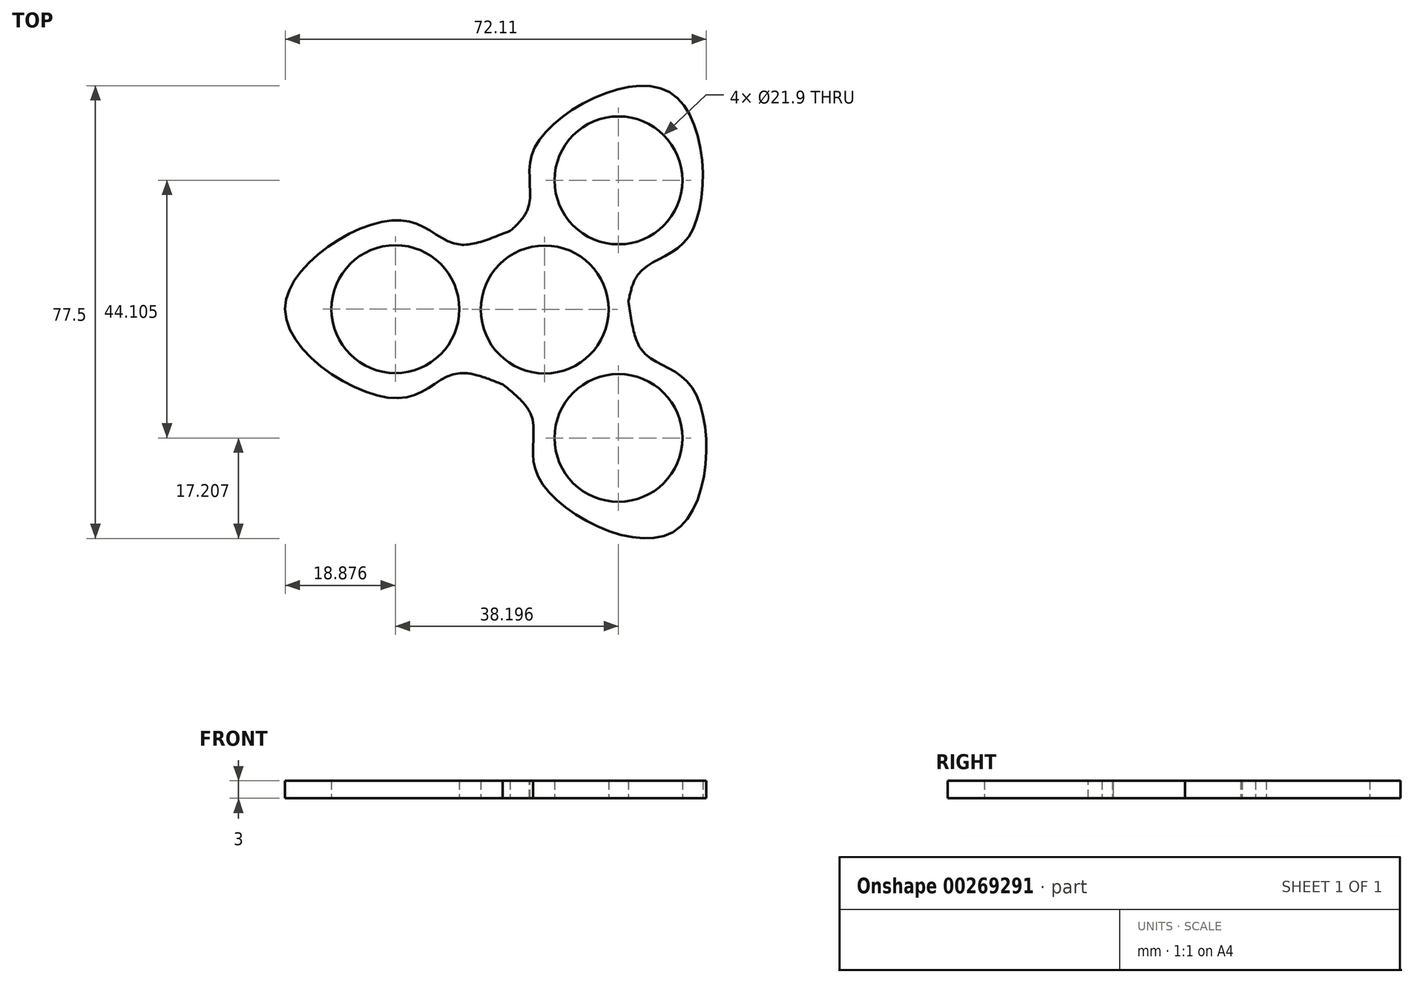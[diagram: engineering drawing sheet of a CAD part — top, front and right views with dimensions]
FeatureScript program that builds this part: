
annotation { "Feature Type Name" : "Feature", "Feature Type Description" : "" }
export const myFeature = defineFeature(function(context is Context, id is Id, definition is map)
    precondition{}
    {
        {
            var Q0;
            Q0=qCreatedBy(makeId("Top.planeOp"),FACE);
            var sketch = newSketch(context, id + "F0", { "sketchPlane" : qUnion([Q0])});
            skLineSegment(sketch, "E0.bottom", {"start": v(-26.42, -36.08) * mm, "end": v(-26.42, -36.08) * mm});
            skLineSegment(sketch, "E0.top", {"start": v(-26.42, -5.6) * mm, "end": v(-26.42, -5.6) * mm});
            skPoint(sketch, "E0.middle", {"position": v(0.1, -0.06) * mm});
            skCircle(sketch, "E1", {"center": v(0.1, -0.06) * mm, "radius": 10.95 * mm});
            skLineSegment(sketch, "E2", {"start": v(0.42, 15.17) * mm, "end": v(0.42, 10.88) * mm, "construction": true});
            skLineSegment(sketch, "E3", {"start": v(-52, -5.6) * mm, "end": v(-52, -5.6) * mm});
            skLineSegment(sketch, "E4", {"start": v(-77.56, -36.08) * mm, "end": v(-77.56, -36.08) * mm});
            skPoint(sketch, "E5", {"position": v(0.42, 10.88) * mm});
            skLineSegment(sketch, "E6", {"start": v(0.42, 10.88) * mm, "end": v(-13.41, 11.04) * mm, "construction": true});
            skLineSegment(sketch, "E7", {"start": v(-77.56, -5.6) * mm, "end": v(-77.56, -5.6) * mm});
            skPoint(sketch, "E8", {"position": v(-14.34, 11.05) * mm});
            skFitSpline(sketch, "E9", {"points": [v(0.1, 14.76) * mm, v(-14.34, 11.05) * mm, v(-25.02, 15.24) * mm, v(-44.34, 0) * mm], "startDerivative": vector(-45.32, 0.62) * mm, "endDerivative": vector(0.12, -55.35) * mm});
            skPoint(sketch, "E10.orphan", {"position": v(-48.35, 15.24) * mm});
            skPoint(sketch, "E11.orphan", {"position": v(-11.05, -15.24) * mm});
            skPoint(sketch, "E12.orphan", {"position": v(-40.34, -15.24) * mm});
            skCircle(sketch, "E13", {"center": v(-25.46, 0) * mm, "radius": 10.95 * mm});
            skCircle(sketch, "E14.1.0", {"center": v(12.73, -22.05) * mm, "radius": 10.95 * mm});
            skCircle(sketch, "E14.2.0", {"center": v(12.73, 22.05) * mm, "radius": 10.95 * mm});
            skPoint(sketch, "E14.center", {"position": v(0, 0) * mm});
            skFitSpline(sketch, "E15", {"points": [v(0.1, -14.76) * mm, v(-14.55, -10.95) * mm, v(-25.02, -15.24) * mm, v(-44.34, 0) * mm], "startDerivative": vector(-45.32, -0.62) * mm, "endDerivative": vector(0.12, 55.35) * mm});
            skLineSegment(sketch, "E16.trimOffspring", {"start": v(-14.34, 11.05) * mm, "end": v(-29.1, 11.23) * mm, "construction": true});
            skFitSpline(sketch, "E17", {"points": [v(12, -8.72) * mm, v(16.04, 5.87) * mm, v(24.99, 12.8) * mm, v(21.45, 37.15) * mm], "startDerivative": vector(23.2, 38.94) * mm, "endDerivative": vector(-48, 27.57) * mm});
            skFitSpline(sketch, "E18", {"points": [v(-13.56, 6.04) * mm, v(-2.93, 16.82) * mm, v(-1.41, 28.04) * mm, v(21.45, 37.15) * mm], "startDerivative": vector(22.13, 39.56) * mm, "endDerivative": vector(47.88, -27.78) * mm});
            skFitSpline(sketch, "E19", {"points": [v(-12.97, -7.06) * mm, v(-2.34, -17.85) * mm, v(-0.82, -29.06) * mm, v(22.04, -38.18) * mm], "startDerivative": vector(22.13, -39.56) * mm, "endDerivative": vector(47.88, 27.78) * mm});
            skFitSpline(sketch, "E20", {"points": [v(12.6, 7.7) * mm, v(16.63, -6.9) * mm, v(25.58, -13.82) * mm, v(22.04, -38.18) * mm], "startDerivative": vector(23.2, -38.94) * mm, "endDerivative": vector(-48, -27.57) * mm});
            skLineSegment(sketch, "E21", {"start": v(-14.34, 11.05) * mm, "end": v(-2.93, 16.82) * mm});
            skLineSegment(sketch, "E22", {"start": v(16.04, 5.87) * mm, "end": v(16.63, -6.9) * mm});
            skLineSegment(sketch, "E23", {"start": v(-2.34, -17.85) * mm, "end": v(-13.12, -10.98) * mm});
            skSolve(sketch);
        }
        {
            var Q0;
            Q0=makeQuery(id+"F0.imprint","IMPRINT",FACE,{"disambiguationData":[TD([[makeQuery(id+"F0.imprint","IMPRINT",EDGE,{"derivedFrom":sQuery(id+"F0.wireOp",EDGE,"E1")}),-1.0]])]});
            extrude(context, id + "F1", {"entities" : qUnion([Q0]), "depth" : 3 * mm});
        }
    });
